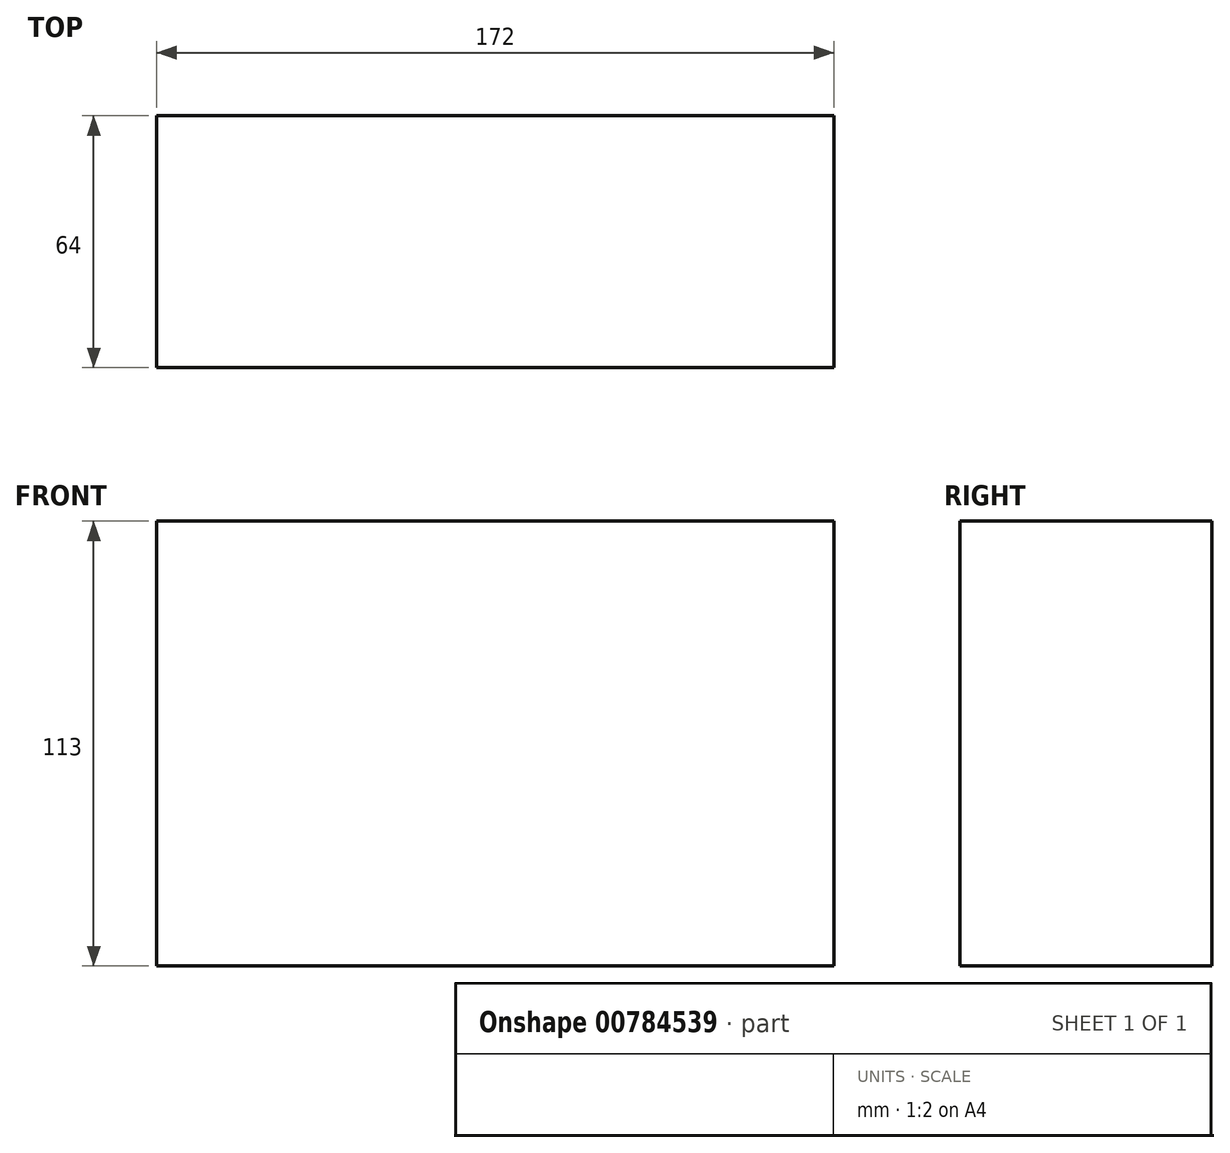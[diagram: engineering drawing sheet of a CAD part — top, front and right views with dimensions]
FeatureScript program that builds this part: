
annotation { "Feature Type Name" : "Feature", "Feature Type Description" : "" }
export const myFeature = defineFeature(function(context is Context, id is Id, definition is map)
    precondition{}
    {
        {
            var Q0;
            Q0=qCreatedBy(makeId("Front.planeOp"),FACE);
            var sketch = newSketch(context, id + "F0", { "sketchPlane" : qUnion([Q0])});
            skLineSegment(sketch, "E0.bottom", {"start": v(0, 0) * mm, "end": v(172, 0) * mm});
            skLineSegment(sketch, "E0.top", {"start": v(0, 113) * mm, "end": v(172, 113) * mm});
            skLineSegment(sketch, "E0.left", {"start": v(0, 0) * mm, "end": v(0, 113) * mm});
            skLineSegment(sketch, "E0.right", {"start": v(172, 0) * mm, "end": v(172, 113) * mm});
            skSolve(sketch);
        }
        {
            var Q0;
            Q0=makeQuery(id+"F0.imprint","IMPRINT",FACE,{"disambiguationData":[TD([[makeQuery(id+"F0.imprint","IMPRINT",EDGE,{"derivedFrom":sQuery(id+"F0.wireOp",EDGE,"E0.bottom")}),1.0]])]});
            extrude(context, id + "F1", {"entities" : qUnion([Q0]), "depth" : 64 * mm, "offsetDistance" : 25 * mm});
        }
    });
